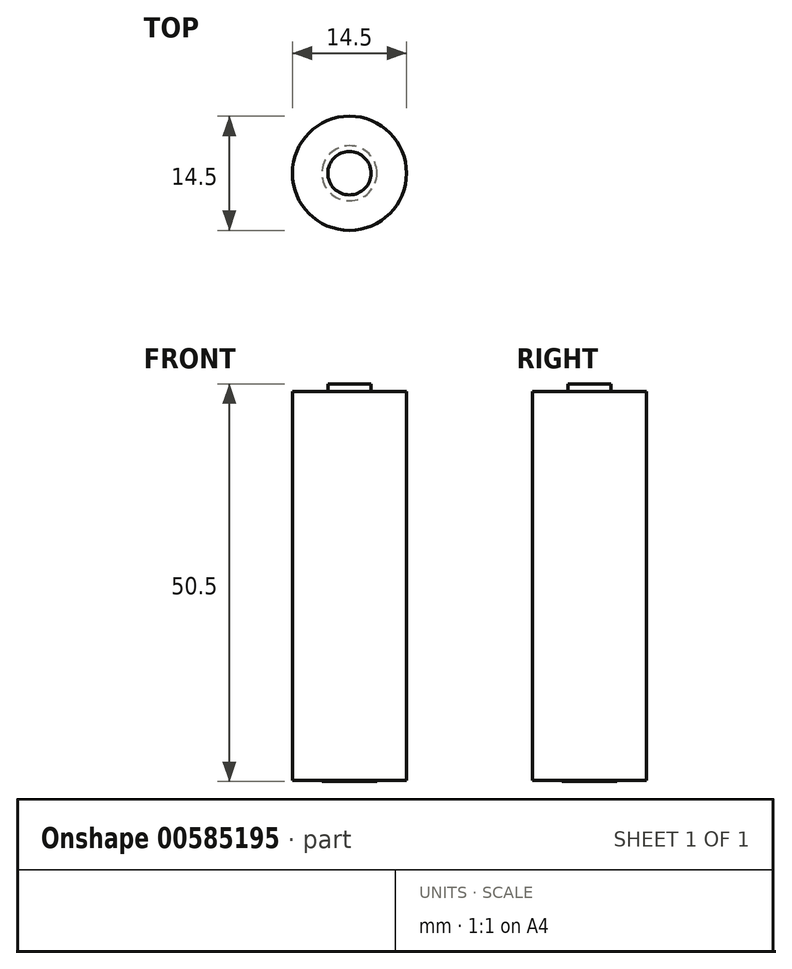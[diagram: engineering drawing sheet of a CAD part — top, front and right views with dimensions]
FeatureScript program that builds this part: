
annotation { "Feature Type Name" : "Feature", "Feature Type Description" : "" }
export const myFeature = defineFeature(function(context is Context, id is Id, definition is map)
    precondition{}
    {
        {
            var Q0;
            Q0=qCreatedBy(makeId("Top.planeOp"),FACE);
            var sketch = newSketch(context, id + "F0", { "sketchPlane" : qUnion([Q0])});
            skCircle(sketch, "E0", {"center": v(0, 0) * mm, "radius": 7.25 * mm});
            skCircle(sketch, "E1", {"center": v(0, 0) * mm, "radius": 3.5 * mm});
            skCircle(sketch, "E2", {"center": v(0, 0) * mm, "radius": 2.75 * mm});
            skSolve(sketch);
        }
        {
            var Q0;
            Q0=makeQuery(id+"F0.imprint","IMPRINT",FACE,{"disambiguationData":[TD([[makeQuery(id+"F0.imprint","IMPRINT",EDGE,{"derivedFrom":sQuery(id+"F0.wireOp",EDGE,"E2")}),1.0]])]});
            extrude(context, id + "F1", {"entities" : qUnion([Q0]), "depth" : 50.5 * mm, "offsetDistance" : 25 * mm});
        }
        {
            var Q0;
            Q0=makeQuery(id+"F0.imprint","IMPRINT",FACE,{"disambiguationData":[TD([[makeQuery(id+"F0.imprint","IMPRINT",EDGE,{"derivedFrom":sQuery(id+"F0.wireOp",EDGE,"E0")}),1.0]])]});
            var Q1;
            Q1=makeQuery(id+"F0.imprint","IMPRINT",FACE,{"disambiguationData":[TD([[makeQuery(id+"F0.imprint","IMPRINT",EDGE,{"derivedFrom":sQuery(id+"F0.wireOp",EDGE,"E1")}),1.0]])]});
            extrude(context, id + "F2", {"entities" : qUnion([Q0, Q1]), "operationType" : NewBodyOperationType.ADD, "depth" : 49.5 * mm, "offsetDistance" : 25 * mm});
        }
        {
            var Q0;
            Q0=makeQuery(id+"F0.imprint","IMPRINT",FACE,{"disambiguationData":[TD([[makeQuery(id+"F0.imprint","IMPRINT",EDGE,{"derivedFrom":sQuery(id+"F0.wireOp",EDGE,"E0")}),1.0]])]});
            extrude(context, id + "F3", {"entities" : qUnion([Q0]), "operationType" : NewBodyOperationType.REMOVE, "depth" : 0.1 * mm, "offsetDistance" : 25 * mm});
        }
    });
